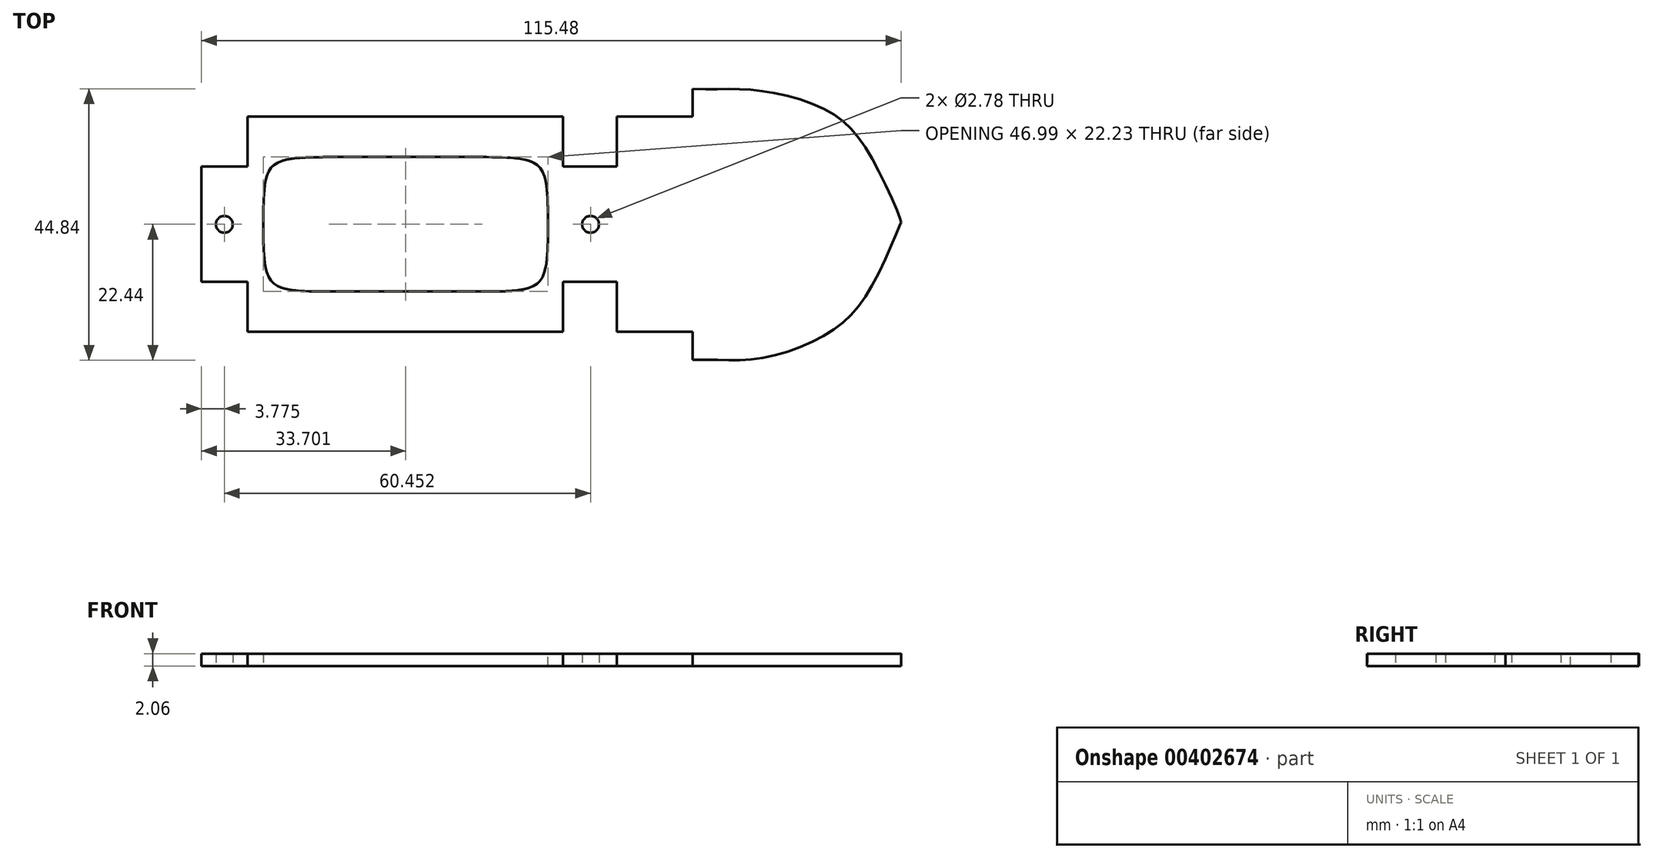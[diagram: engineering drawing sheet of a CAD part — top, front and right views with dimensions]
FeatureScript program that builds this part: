
annotation { "Feature Type Name" : "Feature", "Feature Type Description" : "" }
export const myFeature = defineFeature(function(context is Context, id is Id, definition is map)
    precondition{}
    {
        {
            var Q0;
            Q0=qCreatedBy(makeId("Top.planeOp"),FACE);
            var sketch = newSketch(context, id + "F0", { "sketchPlane" : qUnion([Q0])});
            skLineSegment(sketch, "E0.bottom", {"start": v(50.8, -9.52) * mm, "end": v(-50.8, -9.53) * mm});
            skLineSegment(sketch, "E0.top", {"start": v(50.8, 9.53) * mm, "end": v(-50.8, 9.52) * mm});
            skLineSegment(sketch, "E0.left", {"start": v(50.8, -9.52) * mm, "end": v(50.8, 9.53) * mm});
            skLineSegment(sketch, "E0.right", {"start": v(-50.8, -9.53) * mm, "end": v(-50.8, 9.52) * mm});
            skPoint(sketch, "E0.middle", {"position": v(0, 0) * mm});
            skLineSegment(sketch, "E1.bottom", {"start": v(-43.18, 17.78) * mm, "end": v(8.89, 17.78) * mm});
            skLineSegment(sketch, "E1.top", {"start": v(-43.18, -17.78) * mm, "end": v(8.89, -17.78) * mm});
            skLineSegment(sketch, "E1.left", {"start": v(-43.18, 17.78) * mm, "end": v(-43.18, -17.78) * mm});
            skLineSegment(sketch, "E1.right", {"start": v(8.89, 17.78) * mm, "end": v(8.89, -17.78) * mm});
            skPoint(sketch, "E1.middle", {"position": v(-17.15, 0) * mm});
            skCircle(sketch, "E2", {"center": v(-47.03, 0) * mm, "radius": 1.39 * mm});
            skPoint(sketch, "E2.centerSnap0", {"position": v(-43.18, 0) * mm});
            skCircle(sketch, "E3", {"center": v(13.43, 0) * mm, "radius": 1.39 * mm});
            skSolve(sketch);
        }
        {
            var Q0;
            Q0=qSketchRegion(id+"F0",true);
            extrude(context, id + "F1", {"entities" : qUnion([Q0]), "depth" : 2.06 * mm, "offsetDistance" : 25.4 * mm});
        }
        {
            var Q0;
            Q0=makeQuery(id+"F1.opExtrude","CAP_FACE",FACE,{"disambiguationData":[OSD([sQuery(id+"F0.wireOp",EDGE,"E0.bottom"),sQuery(id+"F0.wireOp",EDGE,"E0.top"),sQuery(id+"F0.wireOp",EDGE,"E0.left"),sQuery(id+"F0.wireOp",EDGE,"E0.right"),sQuery(id+"F0.wireOp",EDGE,"E1.bottom"),sQuery(id+"F0.wireOp",EDGE,"E1.top"),sQuery(id+"F0.wireOp",EDGE,"E1.left"),sQuery(id+"F0.wireOp",EDGE,"E1.right"),sQuery(id+"F0.wireOp",EDGE,"E2"),sQuery(id+"F0.wireOp",EDGE,"E3")])],"isStart":false});
            var sketch = newSketch(context, id + "F2", { "sketchPlane" : qUnion([Q0])});
            skLineSegment(sketch, "E4.bottom", {"start": v(-40.6, 11.11) * mm, "end": v(6.4, 11.11) * mm});
            skLineSegment(sketch, "E4.top", {"start": v(-40.6, -11.11) * mm, "end": v(6.4, -11.11) * mm});
            skLineSegment(sketch, "E4.left", {"start": v(-40.6, 11.11) * mm, "end": v(-40.6, -11.11) * mm});
            skLineSegment(sketch, "E4.right", {"start": v(6.4, 11.11) * mm, "end": v(6.4, -11.11) * mm});
            skSolve(sketch);
        }
        {
            var Q0;
            Q0=makeQuery(id+"F2.imprint","IMPRINT",FACE,{"disambiguationData":[TD([[makeQuery(id+"F2.imprint","IMPRINT",EDGE,{"derivedFrom":sQuery(id+"F2.wireOp",EDGE,"k0T3fhBc-NeAo-Et3q-qg0v-OfHwsomat7l7")}),-1.0]])]});
            var Q1;
            {var subQ0=sQuery(id+"F2.wireOp",EDGE,"dd0a1fe2-3311-4725-ade9-f1b66b535f350.MirrorCS");Q1=makeQuery(id+"F2.imprint","IMPRINT",FACE,{"disambiguationData":[TD([[makeQuery(id+"F2.imprint","IMPRINT",EDGE,{"derivedFrom":subQ0}),1.0]])]});}
            var Q2;
            Q2=makeQuery(id+"F2.imprint","IMPRINT",FACE,{"disambiguationData":[TD([[makeQuery(id+"F2.imprint","IMPRINT",EDGE,{"derivedFrom":sQuery(id+"F2.wireOp",EDGE,"BHx7rwSk-aDuE-Pdrm-xbjg-GFaFYZQyXWyU")}),1.0]])]});
            var Q3;
            Q3=makeQuery(id+"F2.imprint","IMPRINT",FACE,{"disambiguationData":[TD([[makeQuery(id+"F2.imprint","IMPRINT",EDGE,{"derivedFrom":sQuery(id+"F2.wireOp",EDGE,"fsXJdFgY-sX84-sloO-l4Dv-uArRv2zGdPtJ")}),1.0]])]});
            var Q4;
            Q4=makeQuery(id+"F2.imprint","IMPRINT",FACE,{"disambiguationData":[TD([[makeQuery(id+"F2.imprint","IMPRINT",EDGE,{"derivedFrom":sQuery(id+"F2.wireOp",EDGE,"E4.bottom")}),-1.0]])]});
            extrude(context, id + "F3", {"entities" : qUnion([Q0, Q1, Q2, Q3, Q4]), "operationType" : NewBodyOperationType.REMOVE, "oppositeDirection" : true, "depth" : 25.4 * mm});
        }
        {
            var Q0;
            Q0=makeQuery(id+"F3.boolean.opBoolean","COPY",EDGE,{"derivedFrom":makeQuery(id+"F3.opExtrude","SWEPT_EDGE",EDGE,{"disambiguationData":[OSD([sQuery(id+"F2.wireOp",EDGE,"E4.bottom"),sQuery(id+"F2.wireOp",EDGE,"E4.right")])]})});
            var Q1;
            Q1=makeQuery(id+"F3.boolean.opBoolean","COPY",EDGE,{"derivedFrom":makeQuery(id+"F3.opExtrude","SWEPT_EDGE",EDGE,{"disambiguationData":[OSD([sQuery(id+"F2.wireOp",EDGE,"E4.bottom"),sQuery(id+"F2.wireOp",EDGE,"E4.left")])]})});
            var Q2;
            Q2=makeQuery(id+"F3.boolean.opBoolean","COPY",EDGE,{"derivedFrom":makeQuery(id+"F3.opExtrude","SWEPT_EDGE",EDGE,{"disambiguationData":[OSD([sQuery(id+"F2.wireOp",EDGE,"E4.top"),sQuery(id+"F2.wireOp",EDGE,"E4.left")])]})});
            var Q3;
            Q3=makeQuery(id+"F3.boolean.opBoolean","COPY",EDGE,{"derivedFrom":makeQuery(id+"F3.opExtrude","SWEPT_EDGE",EDGE,{"disambiguationData":[OSD([sQuery(id+"F2.wireOp",EDGE,"E4.top"),sQuery(id+"F2.wireOp",EDGE,"E4.right")])]})});
            fillet(context, id + "F4", {"entities" : qUnion([Q0, Q1, Q2, Q3]), "radius" : 10.16 * mm, "tangentPropagation" : true, "rho" : .7, "crossSection" : FilletCrossSection.CONIC, "allowEdgeOverflow" : false});
        }
        {
            var Q0;
            Q0=qCreatedBy(makeId("Top.planeOp"),FACE);
            var sketch = newSketch(context, id + "F5", { "sketchPlane" : qUnion([Q0])});
            skFitSpline(sketch, "E5", {"points": [v(30.28, 22.4) * mm, v(41.02, 22.12) * mm, v(53.24, 18.36) * mm, v(60.42, 9.9) * mm, v(64.67, 0.37) * mm, v(64.55, 0.37) * mm], "startDerivative": vector(52.83, -2) * mm, "endDerivative": vector(-5.96, 2.28) * mm});
            skFitSpline(sketch, "E6.MirrorCS", {"points": [v(30.28, -22.4) * mm, v(41.13, -22.18) * mm, v(53.24, -17.61) * mm, v(60.42, -9.15) * mm, v(64.67, 0.37) * mm, v(64.55, 0.37) * mm], "startDerivative": vector(52.83, 2) * mm, "endDerivative": vector(-13.98, 0) * mm});
            skLineSegment(sketch, "E7", {"start": v(17.78, 0) * mm, "end": v(17.78, -17.78) * mm});
            skLineSegment(sketch, "E8", {"start": v(17.78, -17.78) * mm, "end": v(30.28, -17.78) * mm});
            skLineSegment(sketch, "E9", {"start": v(30.28, -17.78) * mm, "end": v(30.28, -22.4) * mm});
            skLineSegment(sketch, "E10.MirrorCS", {"start": v(17.78, 0) * mm, "end": v(17.78, 17.78) * mm});
            skLineSegment(sketch, "E11.MirrorCS", {"start": v(17.78, 17.78) * mm, "end": v(30.28, 17.78) * mm});
            skLineSegment(sketch, "E12.MirrorCS", {"start": v(30.28, 17.78) * mm, "end": v(30.28, 22.4) * mm});
            skSolve(sketch);
        }
        {
            var Q0;
            Q0 = qSketchRegion(id + "F5", true);
            extrude(context, id + "F6", {"entities" : qUnion([Q0]), "operationType" : NewBodyOperationType.ADD, "depth" : 2.06 * mm, "offsetDistance" : 25.4 * mm});
        }
    });
